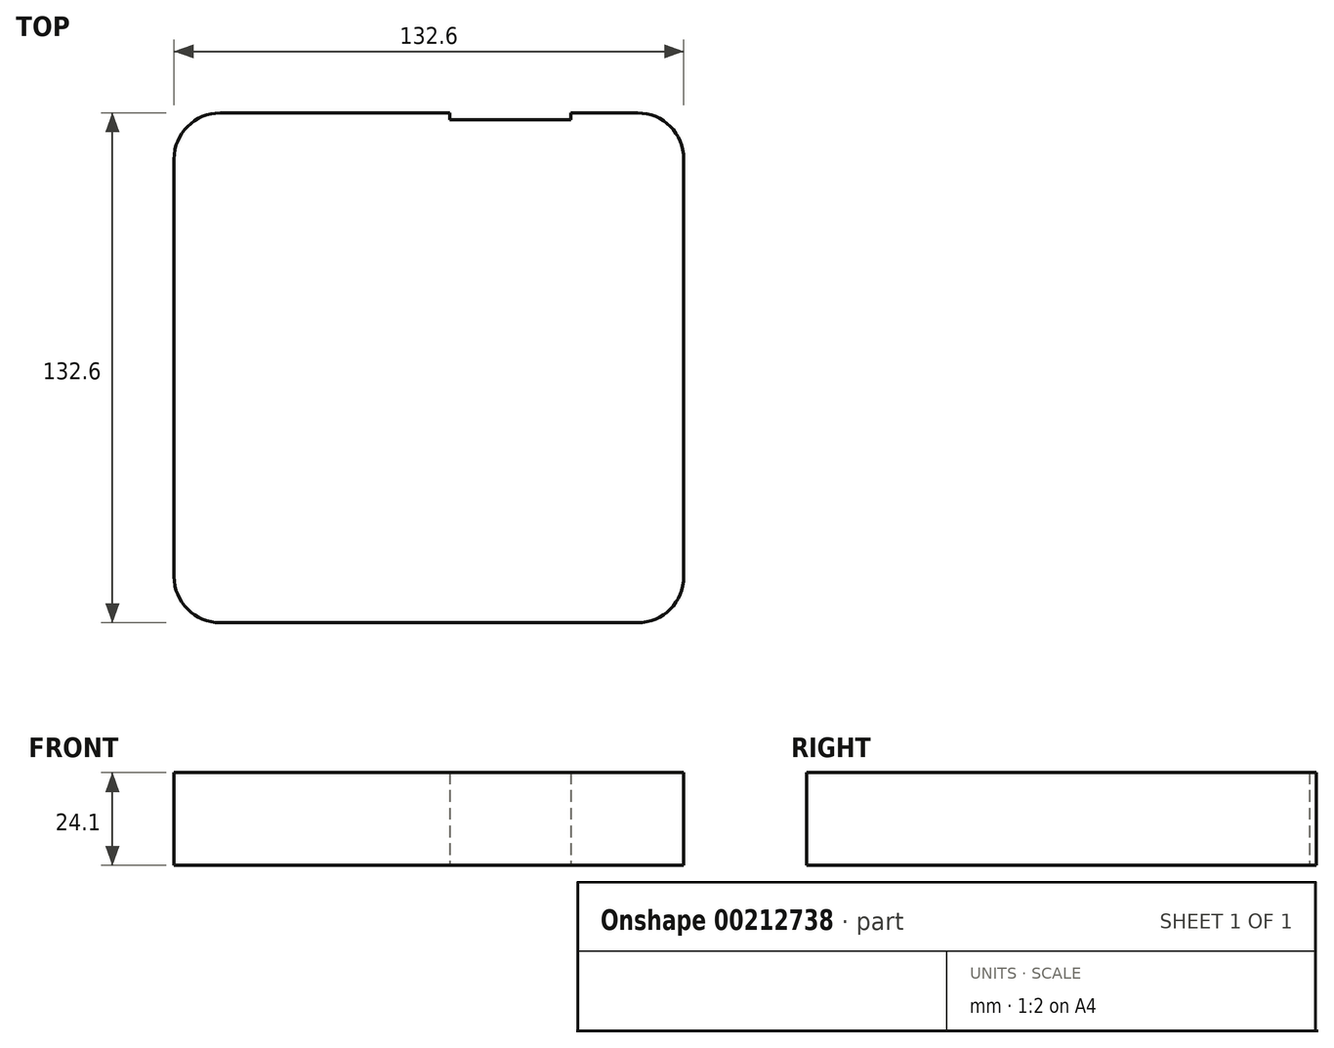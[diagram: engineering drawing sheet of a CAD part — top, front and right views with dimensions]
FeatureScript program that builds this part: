
annotation { "Feature Type Name" : "Feature", "Feature Type Description" : "" }
export const myFeature = defineFeature(function(context is Context, id is Id, definition is map)
    precondition{}
    {
        {
            assignVariable(context, id + "F0", {"name" : "depth", "anyValue" : 24.1});
        }
        {
            var Q0;
            Q0=qCreatedBy(makeId("Top.planeOp"),FACE);
            var sketch = newSketch(context, id + "F1", { "sketchPlane" : qUnion([Q0])});
            skLineSegment(sketch, "E0.bottom", {"start": v(-54.3, 66.3) * mm, "end": v(54.3, 66.3) * mm});
            skLineSegment(sketch, "E0.top", {"start": v(-54.3, -66.3) * mm, "end": v(54.3, -66.3) * mm});
            skLineSegment(sketch, "E0.left", {"start": v(-66.3, 54.3) * mm, "end": v(-66.3, -54.3) * mm});
            skLineSegment(sketch, "E0.right", {"start": v(66.3, 54.3) * mm, "end": v(66.3, -54.3) * mm});
            skPoint(sketch, "E1", {"position": v(-66.3, 0) * mm});
            skPoint(sketch, "E2", {"position": v(5.5, 66.3) * mm});
            skPoint(sketch, "E3", {"position": v(36.9, 66.3) * mm});
            skPoint(sketch, "E4", {"position": v(0, -66.3) * mm});
            skLineSegment(sketch, "E5.bottom", {"start": v(5.5, 66.3) * mm, "end": v(36.9, 66.3) * mm});
            skLineSegment(sketch, "E5.top", {"start": v(5.5, 64.5) * mm, "end": v(36.9, 64.5) * mm});
            skLineSegment(sketch, "E5.left", {"start": v(5.5, 66.3) * mm, "end": v(5.5, 64.5) * mm});
            skLineSegment(sketch, "E5.right", {"start": v(36.9, 66.3) * mm, "end": v(36.9, 64.5) * mm});
            skPoint(sketch, "E6.visualSharp", {"position": v(-66.3, 66.3) * mm});
            skArc(sketch, "E6.filletArc", {"start": v(-54.3, 66.3) * mm, "mid": v(-62.79, 62.79) * mm, "end": v(-66.3, 54.3) * mm});
            skPoint(sketch, "E7.visualSharp", {"position": v(66.3, 66.3) * mm});
            skArc(sketch, "E7.filletArc", {"start": v(66.3, 54.3) * mm, "mid": v(62.79, 62.79) * mm, "end": v(54.3, 66.3) * mm});
            skPoint(sketch, "E8.visualSharp", {"position": v(66.3, -66.3) * mm});
            skArc(sketch, "E8.filletArc", {"start": v(54.3, -66.3) * mm, "mid": v(62.79, -62.79) * mm, "end": v(66.3, -54.3) * mm});
            skPoint(sketch, "E9.visualSharp", {"position": v(-66.3, -66.3) * mm});
            skArc(sketch, "E9.filletArc", {"start": v(-66.3, -54.3) * mm, "mid": v(-62.79, -62.79) * mm, "end": v(-54.3, -66.3) * mm});
            skSolve(sketch);
        }
        {
            var Q0;
            Q0=makeQuery(id+"F1.imprint","IMPRINT",FACE,{"disambiguationData":[TD([[makeQuery(id+"F1.imprint","IMPRINT",EDGE,{"derivedFrom":sQuery(id+"F1.wireOp",EDGE,"E0.top")}),1.0]])]});
            extrude(context, id + "F2", {"entities" : qUnion([Q0]), "depth" : (getVariable(context, 'depth')) * mm});
        }
    });
